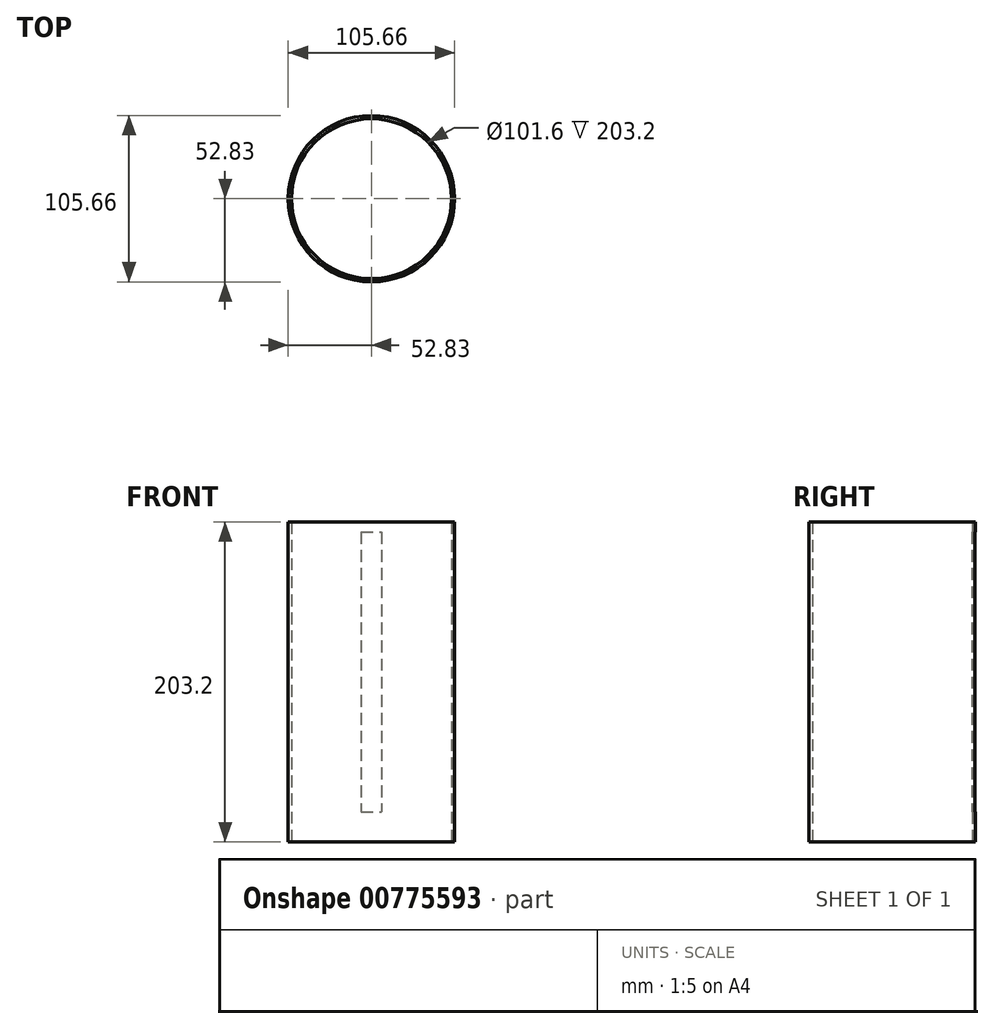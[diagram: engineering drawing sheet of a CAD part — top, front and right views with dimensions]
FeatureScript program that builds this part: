
annotation { "Feature Type Name" : "Feature", "Feature Type Description" : "" }
export const myFeature = defineFeature(function(context is Context, id is Id, definition is map)
    precondition{}
    {
        {
            var Q0;
            Q0=qCreatedBy(makeId("Top.planeOp"),FACE);
            var sketch = newSketch(context, id + "F0", { "sketchPlane" : qUnion([Q0])});
            skCircle(sketch, "E0", {"center": v(0, 0) * mm, "radius": 52.83 * mm});
            skCircle(sketch, "E1", {"center": v(0, 0) * mm, "radius": 50.8 * mm});
            skSolve(sketch);
        }
        {
            var Q0;
            Q0 = qSketchRegion(id + "F0", true);
            extrude(context, id + "F1", {"entities" : qUnion([Q0]), "depth" : 203.2 * mm, "offsetDistance" : 25.4 * mm});
        }
        {
            var Q0;
            Q0=qCreatedBy(makeId("Front.planeOp"),FACE);
            var sketch = newSketch(context, id + "F2", { "sketchPlane" : qUnion([Q0])});
            skLineSegment(sketch, "E2.bottom", {"start": v(-6.48, 196.85) * mm, "end": v(6.48, 196.85) * mm});
            skLineSegment(sketch, "E2.top", {"start": v(-6.48, 19.05) * mm, "end": v(6.48, 19.05) * mm});
            skLineSegment(sketch, "E2.left", {"start": v(-6.48, 196.85) * mm, "end": v(-6.48, 19.05) * mm});
            skLineSegment(sketch, "E2.right", {"start": v(6.48, 196.85) * mm, "end": v(6.48, 19.05) * mm});
            skLineSegment(sketch, "E3", {"start": v(0, 0) * mm, "end": v(0, 240.64) * mm});
            skSolve(sketch);
        }
        {
            var Q0;
            Q0 = qSketchRegion(id + "F2", true);
            extrude(context, id + "F3", {"entities" : qUnion([Q0]), "operationType" : NewBodyOperationType.REMOVE, "oppositeDirection" : true, "depth" : 76.2 * mm, "offsetDistance" : 25.4 * mm});
        }
    });
